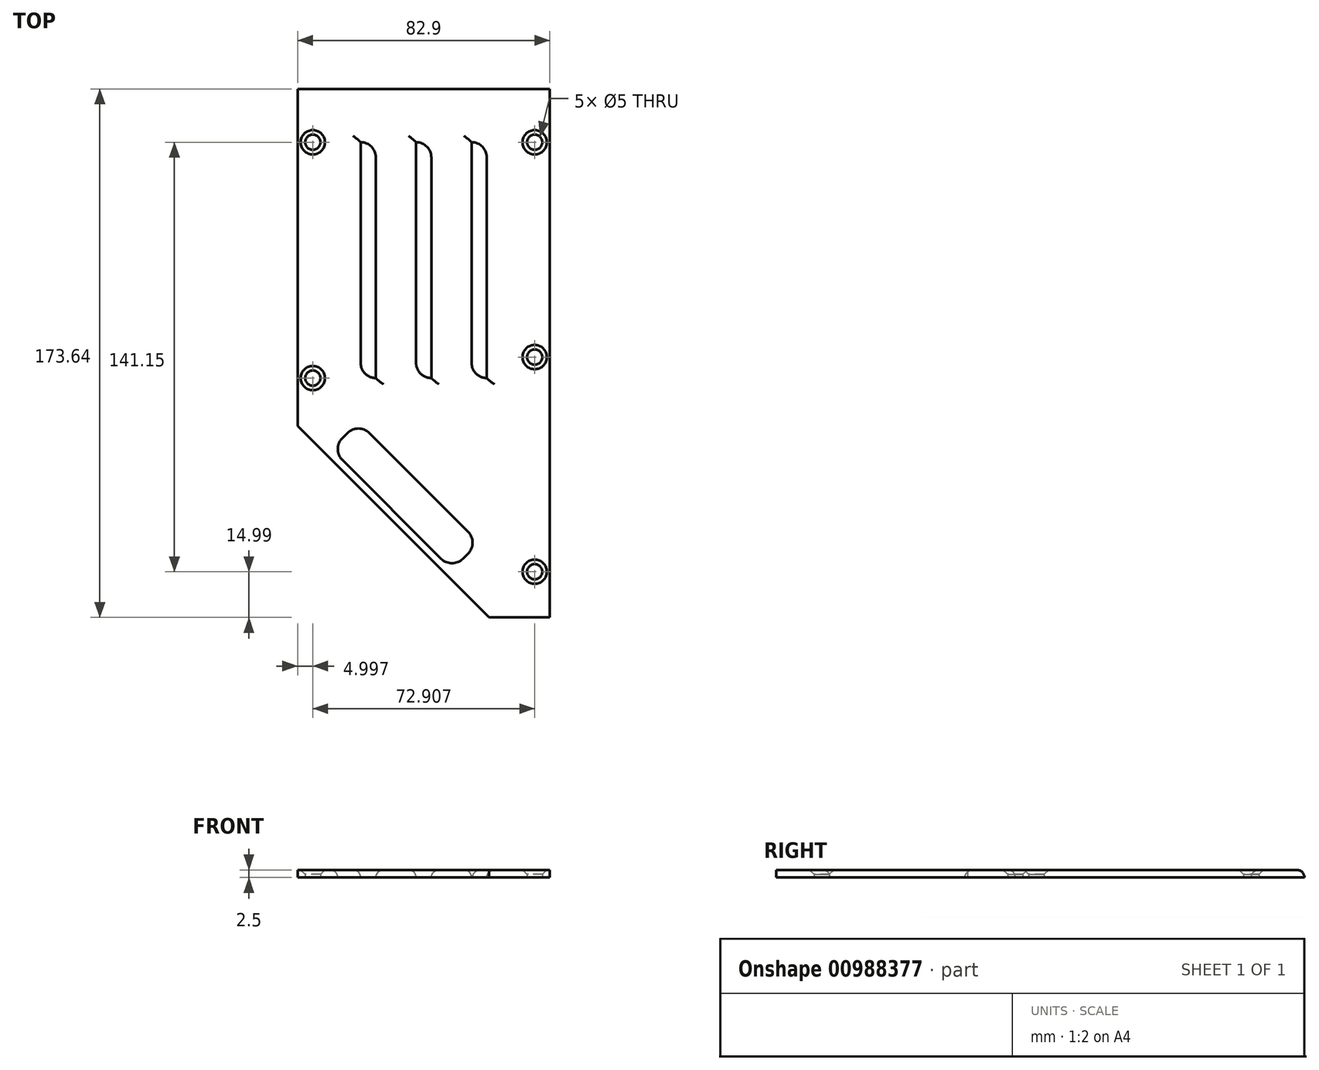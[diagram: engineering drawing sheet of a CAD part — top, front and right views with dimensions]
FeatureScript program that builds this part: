
annotation { "Feature Type Name" : "Feature", "Feature Type Description" : "" }
export const myFeature = defineFeature(function(context is Context, id is Id, definition is map)
    precondition{}
    {
        {
            var Q0;
            Q0=qCreatedBy(makeId("Top.planeOp"),FACE);
            var sketch = newSketch(context, id + "F0", { "sketchPlane" : qUnion([Q0])});
            skPoint(sketch, "E0", {"position": v(-41.45, 86.82) * mm});
            skLineSegment(sketch, "E1.bottom", {"start": v(-41.45, 86.82) * mm, "end": v(41.45, 86.82) * mm});
            skLineSegment(sketch, "E1.top", {"start": v(21.45, -86.82) * mm, "end": v(41.45, -86.82) * mm});
            skLineSegment(sketch, "E1.left", {"start": v(-41.45, 86.82) * mm, "end": v(-41.45, -23.91) * mm});
            skLineSegment(sketch, "E1.right", {"start": v(41.45, 86.82) * mm, "end": v(41.45, -86.82) * mm});
            skLineSegment(sketch, "E2", {"start": v(-41.45, -23.91) * mm, "end": v(21.45, -86.82) * mm});
            skCircle(sketch, "E3", {"center": v(-36.45, 69.32) * mm, "radius": 2.5 * mm});
            skCircle(sketch, "E4", {"center": v(-36.45, -8.18) * mm, "radius": 2.5 * mm});
            skCircle(sketch, "E5", {"center": v(36.45, -71.83) * mm, "radius": 2.5 * mm});
            skCircle(sketch, "E6", {"center": v(36.45, -1.28) * mm, "radius": 2.5 * mm});
            skCircle(sketch, "E7", {"center": v(36.45, 69.32) * mm, "radius": 2.5 * mm});
            skLineSegment(sketch, "E8", {"start": v(-20.73, 69.33) * mm, "end": v(-20.73, -3.2) * mm});
            skLineSegment(sketch, "E9", {"start": v(-15.73, 64.32) * mm, "end": v(-15.73, -8.18) * mm});
            skArc(sketch, "E10", {"start": v(-15.73, 64.32) * mm, "mid": v(-17.2, 67.86) * mm, "end": v(-20.73, 69.33) * mm});
            skArc(sketch, "E11", {"start": v(-20.73, -3.2) * mm, "mid": v(-19.26, -6.73) * mm, "end": v(-15.73, -8.18) * mm});
            skLineSegment(sketch, "E12.1.0.0", {"start": v(-2.5, 69.33) * mm, "end": v(-2.5, -3.2) * mm});
            skArc(sketch, "E12.1.0.1", {"start": v(2.5, 64.32) * mm, "mid": v(1.03, 67.86) * mm, "end": v(-2.5, 69.33) * mm});
            skArc(sketch, "E12.1.0.2", {"start": v(-2.5, -3.2) * mm, "mid": v(-1.04, -6.73) * mm, "end": v(2.5, -8.18) * mm});
            skLineSegment(sketch, "E12.1.0.3", {"start": v(2.5, 64.32) * mm, "end": v(2.5, -8.18) * mm});
            skLineSegment(sketch, "E12.2.0.0", {"start": v(15.72, 69.33) * mm, "end": v(15.72, -3.2) * mm});
            skArc(sketch, "E12.2.0.1", {"start": v(20.72, 64.32) * mm, "mid": v(19.26, 67.86) * mm, "end": v(15.72, 69.33) * mm});
            skArc(sketch, "E12.2.0.2", {"start": v(15.72, -3.2) * mm, "mid": v(17.19, -6.73) * mm, "end": v(20.72, -8.18) * mm});
            skLineSegment(sketch, "E12.2.0.3", {"start": v(20.72, 64.32) * mm, "end": v(20.72, -8.18) * mm});
            skLineSegment(sketch, "E12.direction1", {"start": v(-15.73, -8.18) * mm, "end": v(2.5, -8.18) * mm, "construction": true});
            skLineSegment(sketch, "E13", {"start": v(-17.94, -26.21) * mm, "end": v(14.58, -58.74) * mm});
            skLineSegment(sketch, "E14", {"start": v(-26.78, -35.05) * mm, "end": v(5.75, -67.58) * mm});
            skLineSegment(sketch, "E15", {"start": v(-26.78, -27.98) * mm, "end": v(-25.01, -26.21) * mm});
            skLineSegment(sketch, "E16", {"start": v(12.82, -67.58) * mm, "end": v(14.58, -65.8) * mm});
            skArc(sketch, "E17", {"start": v(-17.94, -26.21) * mm, "mid": v(-21.48, -24.75) * mm, "end": v(-25.01, -26.21) * mm});
            skArc(sketch, "E18", {"start": v(-26.78, -27.98) * mm, "mid": v(-28.25, -31.51) * mm, "end": v(-26.78, -35.05) * mm});
            skArc(sketch, "E19", {"start": v(14.58, -65.8) * mm, "mid": v(16.05, -62.27) * mm, "end": v(14.58, -58.74) * mm});
            skArc(sketch, "E20", {"start": v(5.75, -67.58) * mm, "mid": v(9.28, -69.04) * mm, "end": v(12.82, -67.58) * mm});
            skSolve(sketch);
        }
        {
            var Q0;
            Q0 = qSketchRegion(id + "F0", true);
            extrude(context, id + "F1", {"entities" : qUnion([Q0]), "endBound" : BoundingType.SYMMETRIC, "depth" : 2.5 * mm, "offsetDistance" : 25 * mm});
        }
        {
            var Q0;
            Q0=makeQuery(id+"F1.opExtrude","CAP_EDGE",EDGE,{"disambiguationData":[OSD([sQuery(id+"F0.wireOp",EDGE,"E14")])],"isStart":false});
            var Q1;
            Q1=makeQuery(id+"F1.opExtrude","CAP_EDGE",EDGE,{"disambiguationData":[OSD([sQuery(id+"F0.wireOp",EDGE,"E8")])],"isStart":false});
            var Q2;
            Q2=makeQuery(id+"F1.opExtrude","CAP_EDGE",EDGE,{"disambiguationData":[OSD([sQuery(id+"F0.wireOp",EDGE,"E12.1.0.0")])],"isStart":false});
            var Q3;
            Q3=makeQuery(id+"F1.opExtrude","CAP_EDGE",EDGE,{"disambiguationData":[OSD([sQuery(id+"F0.wireOp",EDGE,"E12.2.0.0")])],"isStart":false});
            var Q4;
            Q4=makeQuery(id+"F1.opExtrude","CAP_EDGE",EDGE,{"disambiguationData":[OSD([sQuery(id+"F0.wireOp",EDGE,"E10")])],"isStart":false});
            var Q5;
            Q5=makeQuery(id+"F1.opExtrude","CAP_EDGE",EDGE,{"disambiguationData":[OSD([sQuery(id+"F0.wireOp",EDGE,"E12.1.0.1")])],"isStart":false});
            var Q6;
            Q6=makeQuery(id+"F1.opExtrude","CAP_EDGE",EDGE,{"disambiguationData":[OSD([sQuery(id+"F0.wireOp",EDGE,"E12.2.0.1")])],"isStart":false});
            var Q7;
            Q7=makeQuery(id+"F1.opExtrude","CAP_EDGE",EDGE,{"disambiguationData":[OSD([sQuery(id+"F0.wireOp",EDGE,"E1.bottom")])],"isStart":false});
            fillet(context, id + "F2", {"entities" : qUnion([Q0, Q1, Q2, Q3, Q4, Q5, Q6, Q7]), "radius" : 2.5 * mm, "tangentPropagation" : true, "allowEdgeOverflow" : false});
        }
        {
            var Q0;
            Q0=makeQuery(id+"F1.opExtrude","CAP_EDGE",EDGE,{"disambiguationData":[OSD([sQuery(id+"F0.wireOp",EDGE,"E4")])],"isStart":false});
            var Q1;
            Q1=makeQuery(id+"F1.opExtrude","CAP_EDGE",EDGE,{"disambiguationData":[OSD([sQuery(id+"F0.wireOp",EDGE,"E3")])],"isStart":false});
            var Q2;
            Q2=makeQuery(id+"F1.opExtrude","CAP_EDGE",EDGE,{"disambiguationData":[OSD([sQuery(id+"F0.wireOp",EDGE,"E7")])],"isStart":false});
            var Q3;
            Q3=makeQuery(id+"F1.opExtrude","CAP_EDGE",EDGE,{"disambiguationData":[OSD([sQuery(id+"F0.wireOp",EDGE,"E6")])],"isStart":false});
            var Q4;
            Q4=makeQuery(id+"F1.opExtrude","CAP_EDGE",EDGE,{"disambiguationData":[OSD([sQuery(id+"F0.wireOp",EDGE,"E5")])],"isStart":false});
            chamfer(context, id + "F3", {"entities" : qUnion([Q0, Q1, Q2, Q3, Q4]), "width" : 1.5 * mm, "tangentPropagation" : true});
        }
    });
